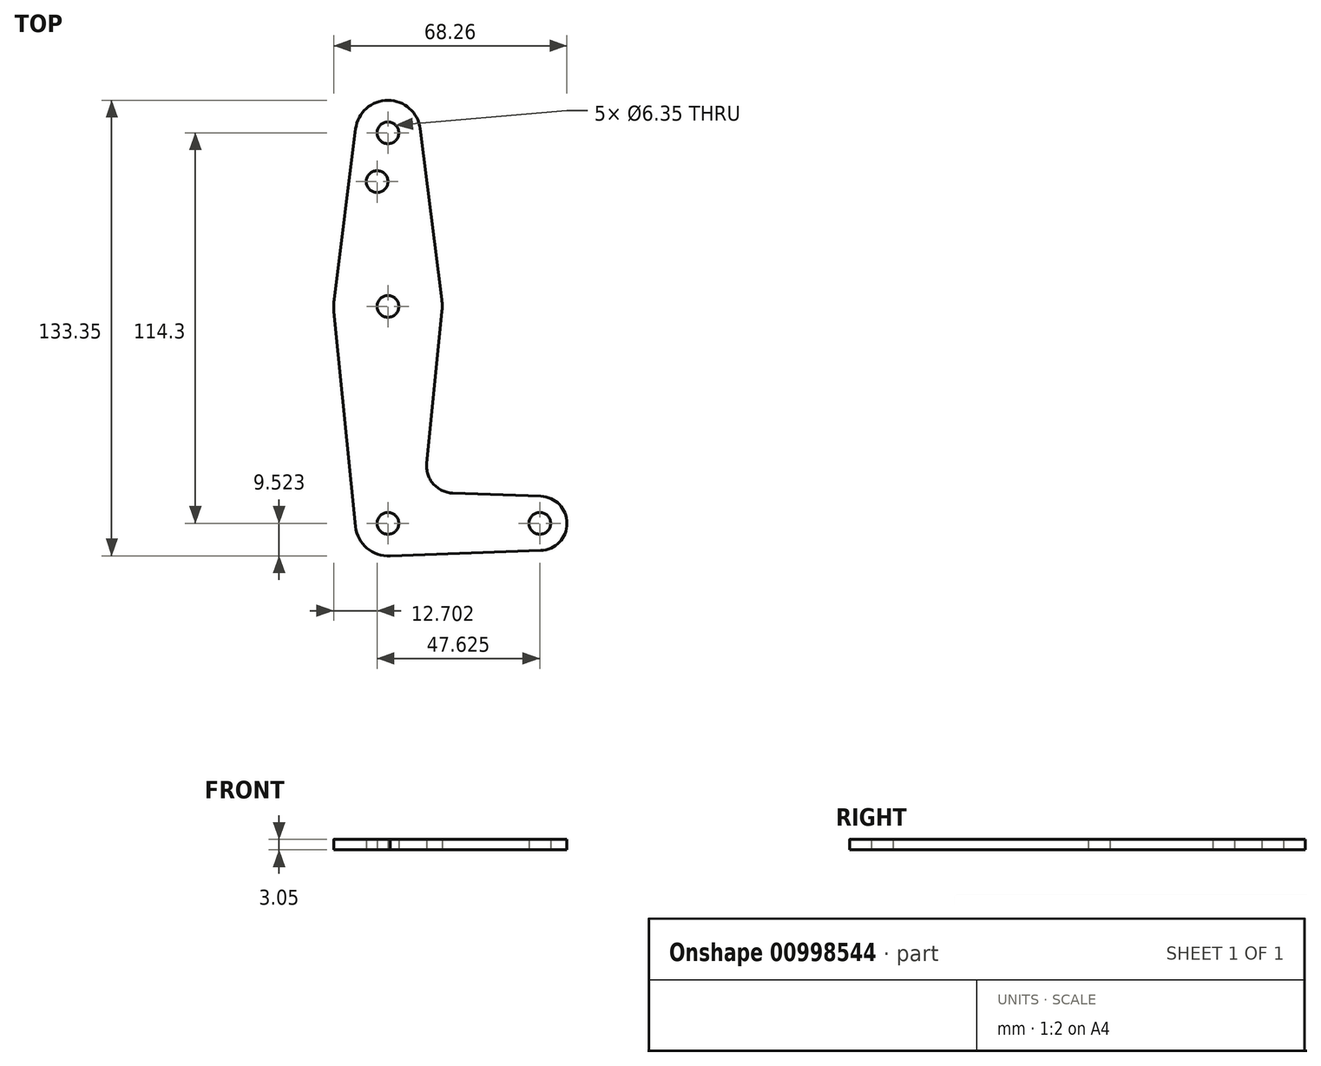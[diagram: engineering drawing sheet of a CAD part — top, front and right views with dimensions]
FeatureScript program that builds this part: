
annotation { "Feature Type Name" : "Feature", "Feature Type Description" : "" }
export const myFeature = defineFeature(function(context is Context, id is Id, definition is map)
    precondition{}
    {
        {
            var Q0;
            Q0=qCreatedBy(makeId("Top.planeOp"),FACE);
            var sketch = newSketch(context, id + "F0", { "sketchPlane" : qUnion([Q0])});
            skLineSegment(sketch, "E0", {"start": v(-217.2, 366.95) * mm, "end": v(-261.64, 366.95) * mm, "construction": true});
            skCircle(sketch, "E1", {"center": v(-261.64, 430.45) * mm, "radius": 15.88 * mm});
            skCircle(sketch, "E2", {"center": v(-261.64, 481.25) * mm, "radius": 9.53 * mm});
            skCircle(sketch, "E3", {"center": v(-261.64, 366.95) * mm, "radius": 9.53 * mm});
            skCircle(sketch, "E4", {"center": v(-217.2, 366.95) * mm, "radius": 7.94 * mm});
            skLineSegment(sketch, "E5", {"start": v(-256.1, 466.78) * mm, "end": v(-261.64, 366.95) * mm, "construction": true});
            skCircle(sketch, "E6", {"center": v(-261.64, 481.25) * mm, "radius": 3.18 * mm});
            skCircle(sketch, "E7", {"center": v(-261.64, 430.45) * mm, "radius": 3.18 * mm});
            skCircle(sketch, "E8", {"center": v(-261.64, 366.95) * mm, "radius": 3.18 * mm});
            skCircle(sketch, "E9", {"center": v(-217.2, 366.95) * mm, "radius": 3.18 * mm});
            skCircle(sketch, "E10", {"center": v(-264.82, 466.98) * mm, "radius": 3.18 * mm});
            skLineSegment(sketch, "E11", {"start": v(-277.44, 428.87) * mm, "end": v(-271.12, 366) * mm});
            skLineSegment(sketch, "E12", {"start": v(-261.64, 357.43) * mm, "end": v(-216.91, 359.02) * mm});
            skLineSegment(sketch, "E13", {"start": v(-216.91, 374.89) * mm, "end": v(-242.68, 375.8) * mm});
            skLineSegment(sketch, "E14", {"start": v(-245.85, 428.87) * mm, "end": v(-250.3, 384.55) * mm});
            skLineSegment(sketch, "E15", {"start": v(-271.1, 482.44) * mm, "end": v(-277.4, 432.44) * mm});
            skLineSegment(sketch, "E16", {"start": v(-252.2, 482.44) * mm, "end": v(-245.9, 432.44) * mm});
            skPoint(sketch, "E17.newPointA", {"position": v(-252.07, 366.95) * mm});
            skPoint(sketch, "E17.newPointB", {"position": v(-261.64, 376.48) * mm});
            skArc(sketch, "E17.filletArc", {"start": v(-250.3, 384.55) * mm, "mid": v(-248.38, 378.52) * mm, "end": v(-242.68, 375.8) * mm});
            skSolve(sketch);
        }
        {
            var Q0;
            Q0 = qSketchRegion(id + "F0", true);
            extrude(context, id + "F1", {"entities" : qUnion([Q0]), "depth" : 3.05 * mm, "offsetDistance" : 25.4 * mm});
        }
    });
